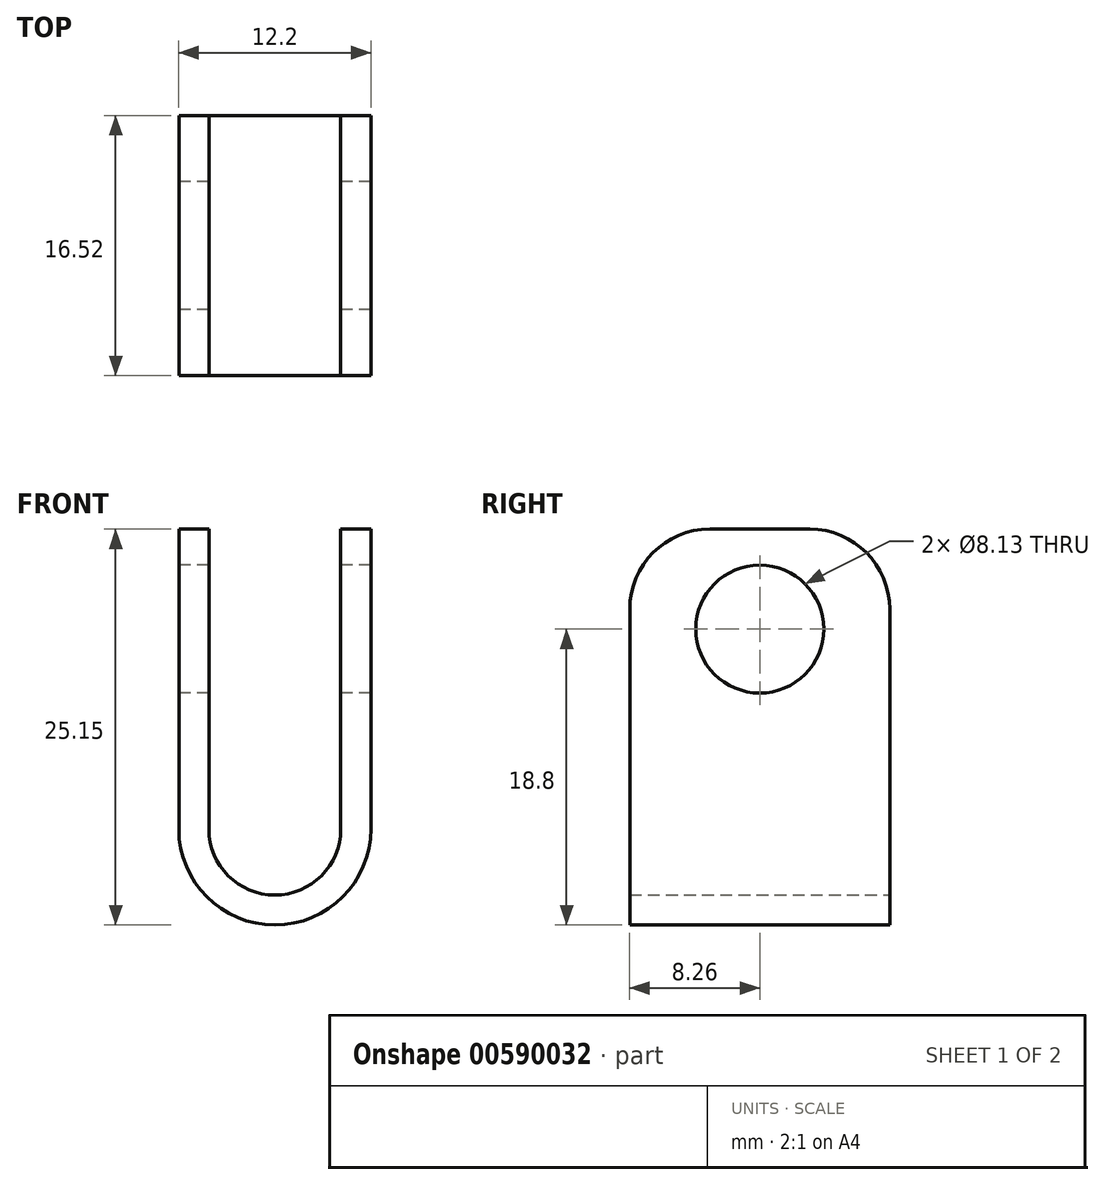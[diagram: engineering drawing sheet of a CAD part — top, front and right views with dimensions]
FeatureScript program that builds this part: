
annotation { "Feature Type Name" : "Feature", "Feature Type Description" : "" }
export const myFeature = defineFeature(function(context is Context, id is Id, definition is map)
    precondition{}
    {
        {
            var Q0;
            Q0=qCreatedBy(makeId("Front.planeOp"),FACE);
            var sketch = newSketch(context, id + "F0", { "sketchPlane" : qUnion([Q0])});
            skArc(sketch, "E0", {"start": v(-4.2, 0) * mm, "mid": v(0, -4.2) * mm, "end": v(4.2, 0) * mm});
            skArc(sketch, "E1", {"start": v(-6.1, 0) * mm, "mid": v(0, -6.1) * mm, "end": v(6.1, 0) * mm});
            skLineSegment(sketch, "E2", {"start": v(-6.1, 0) * mm, "end": v(-6.1, 19.05) * mm});
            skLineSegment(sketch, "E3", {"start": v(6.1, 19.05) * mm, "end": v(6.1, 0) * mm});
            skLineSegment(sketch, "E4", {"start": v(-4.2, 0) * mm, "end": v(-4.2, 19.05) * mm});
            skLineSegment(sketch, "E5", {"start": v(4.2, 0) * mm, "end": v(4.2, 19.05) * mm});
            skLineSegment(sketch, "E6", {"start": v(4.2, 19.05) * mm, "end": v(6.1, 19.05) * mm});
            skLineSegment(sketch, "E7", {"start": v(-6.1, 19.05) * mm, "end": v(-4.2, 19.05) * mm});
            skSolve(sketch);
        }
        {
            var Q0;
            Q0 = qSketchRegion(id + "F0", true);
            extrude(context, id + "F1", {"entities" : qUnion([Q0]), "endBound" : BoundingType.SYMMETRIC, "depth" : 16.5 * mm, "offsetDistance" : 25.4 * mm});
        }
        {
            var Q0;
            Q0=makeQuery(id+"F1.opExtrude","CAP_EDGE",EDGE,{"disambiguationData":[OSD([sQuery(id+"F0.wireOp",EDGE,"E6")])],"isStart":false});
            var Q1;
            Q1=makeQuery(id+"F1.opExtrude","CAP_EDGE",EDGE,{"disambiguationData":[OSD([sQuery(id+"F0.wireOp",EDGE,"E6")])],"isStart":true});
            var Q2;
            Q2=makeQuery(id+"F1.opExtrude","CAP_EDGE",EDGE,{"disambiguationData":[OSD([sQuery(id+"F0.wireOp",EDGE,"E7")])],"isStart":true});
            var Q3;
            Q3=makeQuery(id+"F1.opExtrude","CAP_EDGE",EDGE,{"disambiguationData":[OSD([sQuery(id+"F0.wireOp",EDGE,"E7")])],"isStart":false});
            fillet(context, id + "F2", {"entities" : qUnion([Q0, Q1, Q2, Q3]), "radius" : 5.08 * mm, "tangentPropagation" : true, "allowEdgeOverflow" : false});
        }
        {
            var Q0;
            Q0=qCreatedBy(makeId("Right.planeOp"),FACE);
            var sketch = newSketch(context, id + "F3", { "sketchPlane" : qUnion([Q0])});
            skCircle(sketch, "E8", {"center": v(0, 12.7) * mm, "radius": 4.06 * mm});
            skSolve(sketch);
        }
        {
            var Q0;
            Q0 = qSketchRegion(id + "F3", true);
            extrude(context, id + "F4", {"entities" : qUnion([Q0]), "operationType" : NewBodyOperationType.REMOVE, "endBound" : BoundingType.THROUGH_ALL, "depth" : 25.4 * mm, "offsetDistance" : 25.4 * mm, "hasSecondDirection" : true, "secondDirectionBound" : SecondDirectionBoundingType.THROUGH_ALL, "secondDirectionOppositeDirection" : true, "secondDirectionDepth" : 25.4 * mm});
        }
    });
